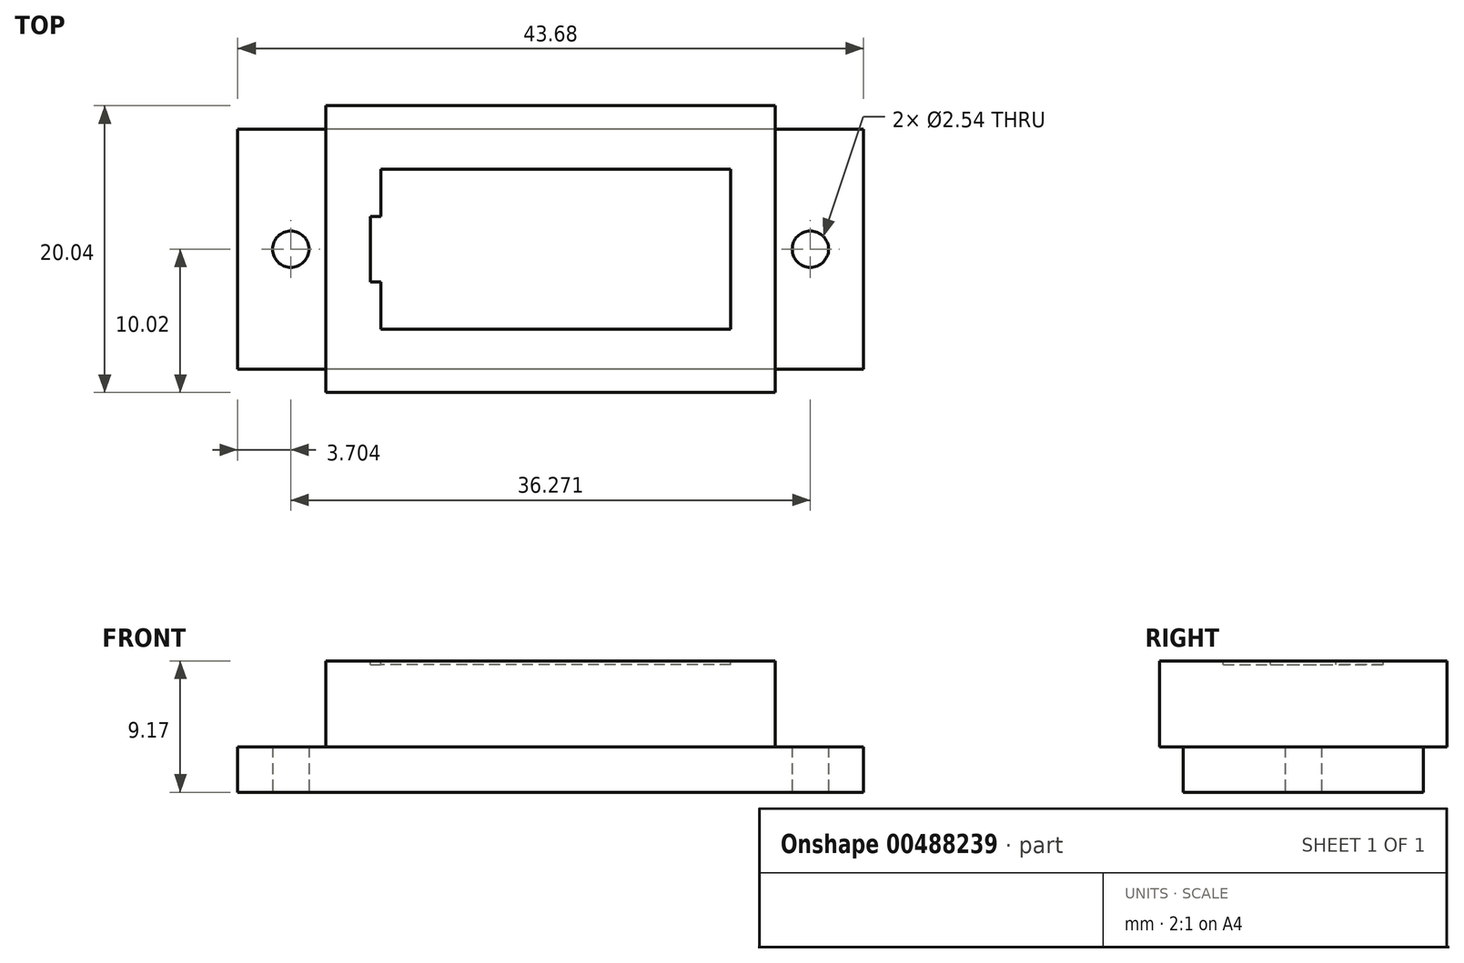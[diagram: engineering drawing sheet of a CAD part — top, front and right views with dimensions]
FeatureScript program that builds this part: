
annotation { "Feature Type Name" : "Feature", "Feature Type Description" : "" }
export const myFeature = defineFeature(function(context is Context, id is Id, definition is map)
    precondition{}
    {
        {
            var Q0;
            Q0=qCreatedBy(makeId("Top.planeOp"),FACE);
            var sketch = newSketch(context, id + "F0", { "sketchPlane" : qUnion([Q0])});
            skLineSegment(sketch, "E0.bottom", {"start": v(21.84, -8.38) * mm, "end": v(-21.84, -8.38) * mm});
            skLineSegment(sketch, "E0.top", {"start": v(21.84, 8.38) * mm, "end": v(-21.84, 8.38) * mm});
            skLineSegment(sketch, "E0.left", {"start": v(21.84, -8.38) * mm, "end": v(21.84, 8.38) * mm});
            skLineSegment(sketch, "E0.right", {"start": v(-21.84, -8.38) * mm, "end": v(-21.84, 8.38) * mm});
            skPoint(sketch, "E0.middle", {"position": v(0, 0) * mm});
            skCircle(sketch, "E1", {"center": v(-18.14, 0) * mm, "radius": 1.27 * mm});
            skCircle(sketch, "E2", {"center": v(18.14, 0) * mm, "radius": 1.27 * mm});
            skSolve(sketch);
        }
        {
            var Q0;
            Q0 = qSketchRegion(id + "F0", true);
            extrude(context, id + "F1", {"entities" : qUnion([Q0]), "depth" : 3.17 * mm, "offsetDistance" : 25.4 * mm});
        }
        {
            var Q0;
            Q0=makeQuery(id+"F1.opExtrude","CAP_FACE",FACE,{"disambiguationData":[OSD([sQuery(id+"F0.wireOp",EDGE,"E0.bottom"),sQuery(id+"F0.wireOp",EDGE,"E0.top"),sQuery(id+"F0.wireOp",EDGE,"E0.left"),sQuery(id+"F0.wireOp",EDGE,"E0.right")])],"isStart":false});
            var sketch = newSketch(context, id + "F2", { "sketchPlane" : qUnion([Q0])});
            skLineSegment(sketch, "E3.bottom", {"start": v(15.68, -10.02) * mm, "end": v(-15.68, -10.02) * mm});
            skLineSegment(sketch, "E3.top", {"start": v(15.68, 10.02) * mm, "end": v(-15.68, 10.02) * mm});
            skLineSegment(sketch, "E3.left", {"start": v(15.68, -10.02) * mm, "end": v(15.68, 10.02) * mm});
            skLineSegment(sketch, "E3.right", {"start": v(-15.68, -10.02) * mm, "end": v(-15.68, 10.02) * mm});
            skPoint(sketch, "E3.middle", {"position": v(0, 0) * mm});
            skSolve(sketch);
        }
        {
            var Q0;
            Q0 = qSketchRegion(id + "F2", true);
            extrude(context, id + "F3", {"entities" : qUnion([Q0]), "operationType" : NewBodyOperationType.ADD, "depth" : 6 * mm, "offsetDistance" : 25.4 * mm});
        }
        {
            var Q0;
            Q0=makeQuery(id+"F3.opExtrude","CAP_FACE",FACE,{"disambiguationData":[OSD([sQuery(id+"F2.wireOp",EDGE,"E3.bottom"),sQuery(id+"F2.wireOp",EDGE,"E3.top"),sQuery(id+"F2.wireOp",EDGE,"E3.left"),sQuery(id+"F2.wireOp",EDGE,"E3.right")])],"isStart":false});
            var sketch = newSketch(context, id + "F4", { "sketchPlane" : qUnion([Q0])});
            skLineSegment(sketch, "E4.bottom", {"start": v(12.57, -5.59) * mm, "end": v(-11.86, -5.59) * mm});
            skLineSegment(sketch, "E4.top", {"start": v(12.57, 5.59) * mm, "end": v(-11.86, 5.59) * mm});
            skLineSegment(sketch, "E4.left", {"start": v(12.57, -5.59) * mm, "end": v(12.57, 5.59) * mm});
            skLineSegment(sketch, "E4.right", {"start": v(-12.57, -2.29) * mm, "end": v(-12.57, 2.29) * mm});
            skPoint(sketch, "E4.middle", {"position": v(0, 0) * mm});
            skLineSegment(sketch, "E5.top", {"start": v(-12.57, 2.29) * mm, "end": v(-11.86, 2.29) * mm});
            skLineSegment(sketch, "E5.right", {"start": v(-11.86, 5.59) * mm, "end": v(-11.86, 2.29) * mm});
            skLineSegment(sketch, "E6.top", {"start": v(-12.57, -2.29) * mm, "end": v(-11.86, -2.29) * mm});
            skLineSegment(sketch, "E6.right", {"start": v(-11.86, -5.59) * mm, "end": v(-11.86, -2.29) * mm});
            skPoint(sketch, "E7.orphan", {"position": v(-12.57, 5.59) * mm});
            skPoint(sketch, "E8.orphan", {"position": v(-12.57, -5.59) * mm});
            skSolve(sketch);
        }
        {
            var Q0;
            Q0 = qSketchRegion(id + "F4", true);
            extrude(context, id + "F5", {"entities" : qUnion([Q0]), "operationType" : NewBodyOperationType.REMOVE, "oppositeDirection" : true, "depth" : 0.25 * mm, "offsetDistance" : 25.4 * mm});
        }
    });
